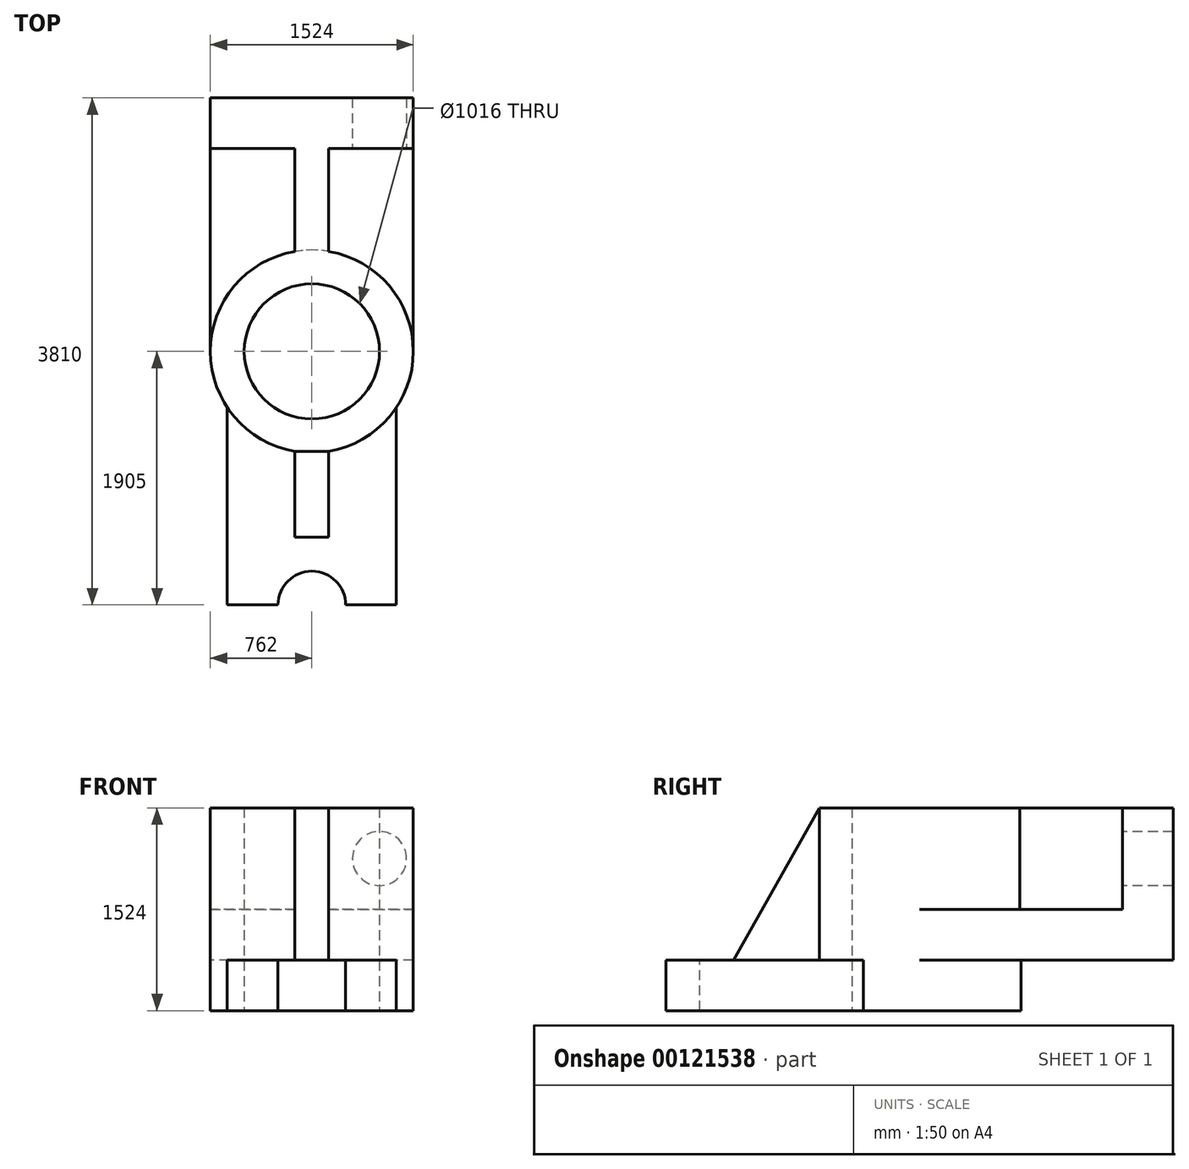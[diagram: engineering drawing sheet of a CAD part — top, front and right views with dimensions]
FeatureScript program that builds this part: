
annotation { "Feature Type Name" : "Feature", "Feature Type Description" : "" }
export const myFeature = defineFeature(function(context is Context, id is Id, definition is map)
    precondition{}
    {
        {
            var Q0;
            Q0=qCreatedBy(makeId("Top.planeOp"),FACE);
            var sketch = newSketch(context, id + "F0", { "sketchPlane" : qUnion([Q0])});
            skLineSegment(sketch, "E0.bottom", {"start": v(762, 1905) * mm, "end": v(-762, 1905) * mm});
            skLineSegment(sketch, "E0.top", {"start": v(762, -1905) * mm, "end": v(-762, -1905) * mm});
            skLineSegment(sketch, "E0.left", {"start": v(762, 1905) * mm, "end": v(762, 0) * mm});
            skLineSegment(sketch, "E0.right", {"start": v(-762, 1905) * mm, "end": v(-762, 0) * mm});
            skPoint(sketch, "E0.middle", {"position": v(0, 0) * mm});
            skLineSegment(sketch, "E1", {"start": v(-762, 1524) * mm, "end": v(762, 1524) * mm});
            skCircle(sketch, "E2", {"center": v(0, 0) * mm, "radius": 762 * mm});
            skCircle(sketch, "E3", {"center": v(0, 0) * mm, "radius": 508 * mm});
            skLineSegment(sketch, "E4.0", {"start": v(-127, 1524) * mm, "end": v(-127, 751.34) * mm});
            skLineSegment(sketch, "E5.0", {"start": v(127, 1524) * mm, "end": v(127, 751.34) * mm});
            skPoint(sketch, "E6.start.orphan", {"position": v(0, 1524) * mm});
            skLineSegment(sketch, "E7", {"start": v(0, 0) * mm, "end": v(0, -1905) * mm});
            skPoint(sketch, "E7.endSnap0", {"position": v(0, -1905) * mm});
            skCircle(sketch, "E8", {"center": v(0, -1905) * mm, "radius": 254 * mm});
            skCircle(sketch, "E9", {"center": v(0, -1905) * mm, "radius": 635 * mm});
            skLineSegment(sketch, "E10", {"start": v(-635, -1905) * mm, "end": v(-635, -421.21) * mm});
            skLineSegment(sketch, "E11", {"start": v(635, -1905) * mm, "end": v(635, -421.21) * mm});
            skPoint(sketch, "E12.orphan", {"position": v(0, -762) * mm});
            skLineSegment(sketch, "E13", {"start": v(127, -1397) * mm, "end": v(127, -751.34) * mm});
            skLineSegment(sketch, "E14.MirrorCS", {"start": v(-127, -1397) * mm, "end": v(-127, -751.34) * mm});
            skLineSegment(sketch, "E15", {"start": v(-127, -1397) * mm, "end": v(127, -1397) * mm});
            skSolve(sketch);
        }
        {
            var Q0;
            {var subQ4=sQuery(id+"F0.wireOp",EDGE,"E0.bottom");Q0=makeQuery(id+"F0.imprint","IMPRINT",FACE,{"disambiguationData":[TD([[makeQuery(id+"F0.imprint","IMPRINT",EDGE,{"derivedFrom":subQ4}),1.0]])]});}
            var Q1;
            {var subQ0=sQuery(id+"F0.wireOp",EDGE,"E4.0");Q1=makeQuery(id+"F0.imprint","IMPRINT",FACE,{"disambiguationData":[TD([[makeQuery(id+"F0.imprint","IMPRINT",EDGE,{"derivedFrom":subQ0}),1.0]])]});}
            var Q2;
            Q2=makeQuery(id+"F0.imprint","IMPRINT",FACE,{"disambiguationData":[TD([[makeQuery(id+"F0.imprint","IMPRINT",EDGE,{"derivedFrom":sQuery(id+"F0.wireOp",EDGE,"E3")}),-1.0]])]});
            extrude(context, id + "F1", {"entities" : qUnion([Q0, Q1, Q2]), "depth" : 1143 * mm, "offsetDistance" : 25.4 * mm});
        }
        {
            var Q0;
            {var subQ5=sQuery(id+"F0.wireOp",EDGE,"E4.0");Q0=makeQuery(id+"F0.imprint","IMPRINT",FACE,{"disambiguationData":[TD([[makeQuery(id+"F0.imprint","IMPRINT",EDGE,{"derivedFrom":subQ5}),-1.0]])]});}
            var Q1;
            {var subQ5=sQuery(id+"F0.wireOp",EDGE,"E5.0");Q1=makeQuery(id+"F0.imprint","IMPRINT",FACE,{"disambiguationData":[TD([[makeQuery(id+"F0.imprint","IMPRINT",EDGE,{"derivedFrom":subQ5}),1.0]])]});}
            extrude(context, id + "F2", {"entities" : qUnion([Q0, Q1]), "operationType" : NewBodyOperationType.ADD, "depth" : 381 * mm, "offsetDistance" : 25.4 * mm});
        }
        {
            var Q0;
            {var subQ4=sQuery(id+"F0.wireOp",EDGE,"E11");Q0=makeQuery(id+"F0.imprint","IMPRINT",FACE,{"disambiguationData":[TD([[makeQuery(id+"F0.imprint","IMPRINT",EDGE,{"derivedFrom":subQ4}),1.0]])]});}
            var Q1;
            {var subQ6=sQuery(id+"F0.wireOp",EDGE,"E10");Q1=makeQuery(id+"F0.imprint","IMPRINT",FACE,{"disambiguationData":[TD([[makeQuery(id+"F0.imprint","IMPRINT",EDGE,{"derivedFrom":subQ6}),-1.0]])]});}
            var Q2;
            {var subQ5=sQuery(id+"F0.wireOp",EDGE,"E9");var subQ7=makeQuery(id+"F0.imprint","IMPRINT",VERTEX,{"disambiguationData":[OD(0.0)],"derivedFrom":subQ5});Q2=makeQuery(id+"F0.imprint","IMPRINT",FACE,{"disambiguationData":[TD([[makeQuery(id+"F0.imprint","IMPRINT",EDGE,{"disambiguationData":[TD([[subQ7,-1.0]])],"derivedFrom":subQ5}),1.0]])]});}
            var Q3;
            {var subQ1=sQuery(id+"F0.wireOp",EDGE,"E0.top");var subQ3=sQuery(id+"F0.wireOp",EDGE,"E8");var subQ4=makeQuery(id+"F0.imprint","INTERSECT",VERTEX,{"disambiguationData":[OD(0.0)],"derivedFrom":[subQ1,subQ3]});Q3=makeQuery(id+"F0.imprint","IMPRINT",FACE,{"disambiguationData":[TD([[makeQuery(id+"F0.imprint","IMPRINT",EDGE,{"disambiguationData":[TD([[subQ4,1.0]])],"derivedFrom":subQ3}),-1.0]])]});}
            var Q4;
            {var subQ0=sQuery(id+"F0.wireOp",EDGE,"E9");var subQ1=makeQuery(id+"F0.imprint","IMPRINT",VERTEX,{"disambiguationData":[OD(1.0)],"derivedFrom":subQ0});Q4=makeQuery(id+"F0.imprint","IMPRINT",FACE,{"disambiguationData":[TD([[makeQuery(id+"F0.imprint","IMPRINT",EDGE,{"disambiguationData":[TD([[subQ1,1.0]])],"derivedFrom":subQ0}),1.0]])]});}
            var Q5;
            Q5=makeQuery(id+"F0.imprint","IMPRINT",FACE,{"disambiguationData":[TD([[makeQuery(id+"F0.imprint","IMPRINT",EDGE,{"derivedFrom":sQuery(id+"F0.wireOp",EDGE,"E3")}),-1.0]])]});
            var Q6;
            {var subQ3=sQuery(id+"F0.wireOp",EDGE,"E7");var subQ9=sQuery(id+"F0.wireOp",EDGE,"E15");var subQ10=makeQuery(id+"F0.imprint","INTERSECT",VERTEX,{"derivedFrom":[subQ3,subQ9]});Q6=makeQuery(id+"F0.imprint","IMPRINT",FACE,{"disambiguationData":[TD([[makeQuery(id+"F0.imprint","IMPRINT",EDGE,{"disambiguationData":[TD([[subQ10,-1.0]])],"derivedFrom":subQ3}),1.0]])]});}
            var Q7;
            {var subQ0=sQuery(id+"F0.wireOp",EDGE,"E15");var subQ1=sQuery(id+"F0.wireOp",EDGE,"E7");var subQ2=makeQuery(id+"F0.imprint","INTERSECT",VERTEX,{"derivedFrom":[subQ1,subQ0]});Q7=makeQuery(id+"F0.imprint","IMPRINT",FACE,{"disambiguationData":[TD([[makeQuery(id+"F0.imprint","IMPRINT",EDGE,{"disambiguationData":[TD([[subQ2,-1.0]])],"derivedFrom":subQ1}),-1.0]])]});}
            var Q8;
            {var subQ0=sQuery(id+"F0.wireOp",EDGE,"E13");var subQ1=sQuery(id+"F0.wireOp",EDGE,"E2");var subQ2=makeQuery(id+"F0.imprint","INTERSECT",VERTEX,{"derivedFrom":[subQ1,subQ0]});Q8=makeQuery(id+"F0.imprint","IMPRINT",FACE,{"disambiguationData":[TD([[makeQuery(id+"F0.imprint","IMPRINT",EDGE,{"disambiguationData":[TD([[subQ2,1.0]])],"derivedFrom":subQ1}),-1.0]])]});}
            var Q9;
            {var subQ0=sQuery(id+"F0.wireOp",EDGE,"E14.MirrorCS");var subQ1=sQuery(id+"F0.wireOp",EDGE,"E2");var subQ2=makeQuery(id+"F0.imprint","INTERSECT",VERTEX,{"derivedFrom":[subQ1,subQ0]});Q9=makeQuery(id+"F0.imprint","IMPRINT",FACE,{"disambiguationData":[TD([[makeQuery(id+"F0.imprint","IMPRINT",EDGE,{"disambiguationData":[TD([[subQ2,-1.0]])],"derivedFrom":subQ1}),-1.0]])]});}
            var Q10;
            {var subQ0=sQuery(id+"F0.wireOp",EDGE,"E9");var subQ1=sQuery(id+"F0.wireOp",EDGE,"E7");var subQ2=makeQuery(id+"F0.imprint","INTERSECT",VERTEX,{"derivedFrom":[subQ1,subQ0]});Q10=makeQuery(id+"F0.imprint","IMPRINT",FACE,{"disambiguationData":[TD([[makeQuery(id+"F0.imprint","IMPRINT",EDGE,{"disambiguationData":[TD([[subQ2,-1.0]])],"derivedFrom":subQ1}),1.0]])]});}
            var Q11;
            {var subQ0=sQuery(id+"F0.wireOp",EDGE,"E9");var subQ1=sQuery(id+"F0.wireOp",EDGE,"E7");var subQ2=makeQuery(id+"F0.imprint","INTERSECT",VERTEX,{"derivedFrom":[subQ1,subQ0]});Q11=makeQuery(id+"F0.imprint","IMPRINT",FACE,{"disambiguationData":[TD([[makeQuery(id+"F0.imprint","IMPRINT",EDGE,{"disambiguationData":[TD([[subQ2,-1.0]])],"derivedFrom":subQ1}),-1.0]])]});}
            extrude(context, id + "F3", {"entities" : qUnion([Q0, Q1, Q2, Q3, Q4, Q5, Q6, Q7, Q8, Q9, Q10, Q11]), "operationType" : NewBodyOperationType.ADD, "oppositeDirection" : true, "depth" : 381 * mm, "offsetDistance" : 25.4 * mm});
        }
        {
            var Q0;
            {var subQ0=sQuery(id+"F0.wireOp",EDGE,"E14.MirrorCS");var subQ1=sQuery(id+"F0.wireOp",EDGE,"E2");var subQ2=makeQuery(id+"F0.imprint","INTERSECT",VERTEX,{"derivedFrom":[subQ1,subQ0]});Q0=makeQuery(id+"F0.imprint","IMPRINT",FACE,{"disambiguationData":[TD([[makeQuery(id+"F0.imprint","IMPRINT",EDGE,{"disambiguationData":[TD([[subQ2,-1.0]])],"derivedFrom":subQ1}),-1.0]])]});}
            var Q1;
            {var subQ0=sQuery(id+"F0.wireOp",EDGE,"E13");var subQ1=sQuery(id+"F0.wireOp",EDGE,"E2");var subQ2=makeQuery(id+"F0.imprint","INTERSECT",VERTEX,{"derivedFrom":[subQ1,subQ0]});Q1=makeQuery(id+"F0.imprint","IMPRINT",FACE,{"disambiguationData":[TD([[makeQuery(id+"F0.imprint","IMPRINT",EDGE,{"disambiguationData":[TD([[subQ2,1.0]])],"derivedFrom":subQ1}),-1.0]])]});}
            var Q2;
            {var subQ0=sQuery(id+"F0.wireOp",EDGE,"E9");var subQ1=sQuery(id+"F0.wireOp",EDGE,"E7");var subQ2=makeQuery(id+"F0.imprint","INTERSECT",VERTEX,{"derivedFrom":[subQ1,subQ0]});Q2=makeQuery(id+"F0.imprint","IMPRINT",FACE,{"disambiguationData":[TD([[makeQuery(id+"F0.imprint","IMPRINT",EDGE,{"disambiguationData":[TD([[subQ2,-1.0]])],"derivedFrom":subQ1}),1.0]])]});}
            var Q3;
            {var subQ0=sQuery(id+"F0.wireOp",EDGE,"E9");var subQ1=sQuery(id+"F0.wireOp",EDGE,"E7");var subQ2=makeQuery(id+"F0.imprint","INTERSECT",VERTEX,{"derivedFrom":[subQ1,subQ0]});Q3=makeQuery(id+"F0.imprint","IMPRINT",FACE,{"disambiguationData":[TD([[makeQuery(id+"F0.imprint","IMPRINT",EDGE,{"disambiguationData":[TD([[subQ2,-1.0]])],"derivedFrom":subQ1}),-1.0]])]});}
            extrude(context, id + "F4", {"entities" : qUnion([Q0, Q1, Q2, Q3]), "operationType" : NewBodyOperationType.ADD, "depth" : 1143 * mm, "offsetDistance" : 25.4 * mm});
        }
        {
            var Q0;
            Q0=makeQuery(id+"F4.opExtrude","SWEPT_FACE",FACE,{"disambiguationData":[OSD([sQuery(id+"F0.wireOp",EDGE,"E13")])]});
            var sketch = newSketch(context, id + "F5", { "sketchPlane" : qUnion([Q0])});
            skLineSegment(sketch, "E16", {"start": v(-751.34, 1143) * mm, "end": v(-1397, 0) * mm});
            skSolve(sketch);
        }
        {
            var Q0;
            Q0=makeQuery(id+"F5.imprint","IMPRINT",FACE,{"disambiguationData":[TD([[makeQuery(id+"F5.imprint","IMPRINT",EDGE,{"derivedFrom":sQuery(id+"F5.wireOp",EDGE,"E16")}),-1.0]])]});
            extrude(context, id + "F6", {"entities" : qUnion([Q0]), "operationType" : NewBodyOperationType.REMOVE, "endBound" : BoundingType.UP_TO_NEXT, "oppositeDirection" : true, "depth" : 25.4 * mm, "offsetDistance" : 25.4 * mm});
        }
        {
            var Q0;
            {var subQ0=sQuery(id+"F0.wireOp",EDGE,"E1");Q0=makeQuery(id+"F1.opExtrude","SWEPT_FACE",FACE,{"disambiguationData":[OSD([subQ0]),TDD([makeQuery(id+"F0.imprint","IMPRINT",EDGE,{"disambiguationData":[TD([[makeQuery(id+"F0.imprint","INTERSECT",VERTEX,{"derivedFrom":[sQuery(id+"F0.wireOp",EDGE,"E0.left"),subQ0]}),1.0]])],"derivedFrom":subQ0})])]});}
            var sketch = newSketch(context, id + "F7", { "sketchPlane" : qUnion([Q0])});
            skLineSegment(sketch, "E17", {"start": v(127, 1143) * mm, "end": v(508, 1143) * mm});
            skLineSegment(sketch, "E18", {"start": v(508, 1143) * mm, "end": v(-381, 1143) * mm, "construction": true});
            skLineSegment(sketch, "E19", {"start": v(508, 1143) * mm, "end": v(508, 762) * mm, "construction": true});
            skCircle(sketch, "E20", {"center": v(508, 762) * mm, "radius": 203.2 * mm});
            skLineSegment(sketch, "E21", {"start": v(0, 1143) * mm, "end": v(0, 368.55) * mm, "construction": true});
            skCircle(sketch, "E22.MirrorC", {"center": v(-508, 762) * mm, "radius": 203.2 * mm});
            skSolve(sketch);
        }
        {
            var Q0;
            Q0=makeQuery(id+"F7.imprint","IMPRINT",FACE,{"disambiguationData":[TD([[makeQuery(id+"F7.imprint","IMPRINT",EDGE,{"derivedFrom":sQuery(id+"F7.wireOp",EDGE,"E20")}),1.0]])]});
            var Q1;
            Q1=makeQuery(id+"F7.imprint","IMPRINT",FACE,{"disambiguationData":[TD([[makeQuery(id+"F7.imprint","IMPRINT",EDGE,{"derivedFrom":sQuery(id+"F7.wireOp",EDGE,"E22.MirrorC")}),-1.0]])]});
            extrude(context, id + "F8", {"entities" : qUnion([Q0, Q1]), "operationType" : NewBodyOperationType.REMOVE, "endBound" : BoundingType.UP_TO_NEXT, "oppositeDirection" : true, "depth" : 25.4 * mm, "offsetDistance" : 25.4 * mm});
        }
    });
